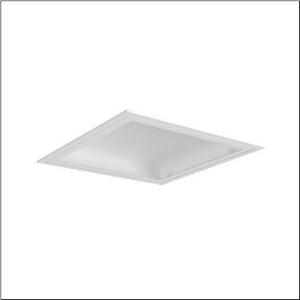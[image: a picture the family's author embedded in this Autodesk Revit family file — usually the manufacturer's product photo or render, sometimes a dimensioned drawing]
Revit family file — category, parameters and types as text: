
# Revit family: mira_r__21_51fr427a432a_cde4
name_source: partatom
category: Lighting Fixtures
units: mm (PartAtom-declared; Revit-internal decimal feet)

## family parameters
Cut with Voids When Loaded = No
Host = Face
Light Source = No
Part Type = Normal
Room Calculation Point = No
Round Connector Dimension = Use Diameter
Shared = No

## types (1)
- Mira® 21 (1 x LED, 3220 lm, 23 W, 4000K)
    Apparent Load = 23 VA
    CIE Flux Codes = 50 81 97 100 100
    Color Rendering = 80
    Color Temperature = 4000K
    Default Elevation = 1800 mm
    Description = Mira® 21, clean room luminaire, primary light control with reflector, primary optical cover: cover, of PC, light emission: direct distribution, primary light characteristic: symmetric, installation type: recessed, LED, rated luminous flux: 3.220lm, luminous efficacy: 140lm/W, light colour: 840, colour temperature: 4000K, control gear: ON/OFF, with terminal, 3-pole, max. 2.5mm², mains connection: 230V, AC, 50/60Hz, rated input power: 23W, luminaire housing, of sheet steel, coated, pure white (RAL 9010), with concealed spring brackets, module: M625, length: 623mm, width: 623mm, height: 115mm, protection rating (complete): IP54, insulation class (complete): insulation class I (protective earthing), certification: CE, UKCA, permissible operating ambient temperature: -5..+40°C, standard: EN 50419, packaging unit: 1 piece
    Height = 0 mm  [stored 0 ft]
    Lamp = 1 x LED
    Lamp Light Flux = 3220 lm
    Lamp Power = 23 W
    Lamp count = 1
    Length = 625 mm
    Luminous efficacy = 140 lm/W
    Manufacturer = Siteco
    ModVariant = No
    Model = 51FR427A432A
    Mounting Place = Ceiling
    Mounting Type = Recessed
    Number of Poles = 1
    OnlyDefault = Yes
    Power Factor = 1
    Product Name = Mira® 21
    Product group = clean room luminaire | ceiling recessed
    ProductGroupID = 402
    Protection Class = Protection class I
    Protection Degree = IP 54
    RLX_Detail_Level = 1
    RLX_Emergency_Light_Flux = 0 lm
    RLX_Emergency_Type = 0
    RLX_Emergency_Type_DB = No
    RlxData = <blob elided: 13397 chars, md5=2e3dccc6>
    Socket = socket
    Standby Power = 0 W
    System Light Flux = 3220 lm
    System Power = 23 W
    Type Comments = Product without accessories
    Type Image = l_1007109.jpg
    URL = http://relux.com
    VarID = ---
    Voltage = 0 V
    Weight = 0.00 kg
    Width = 625 mm

note: [stored X ft] marks values corroborated as IEEE doubles in the binary element streams (Revit-internal decimal feet)

## geometry (parser evidence)
native form markers: Sweep x9
no freeform markers — native parametric forms only
